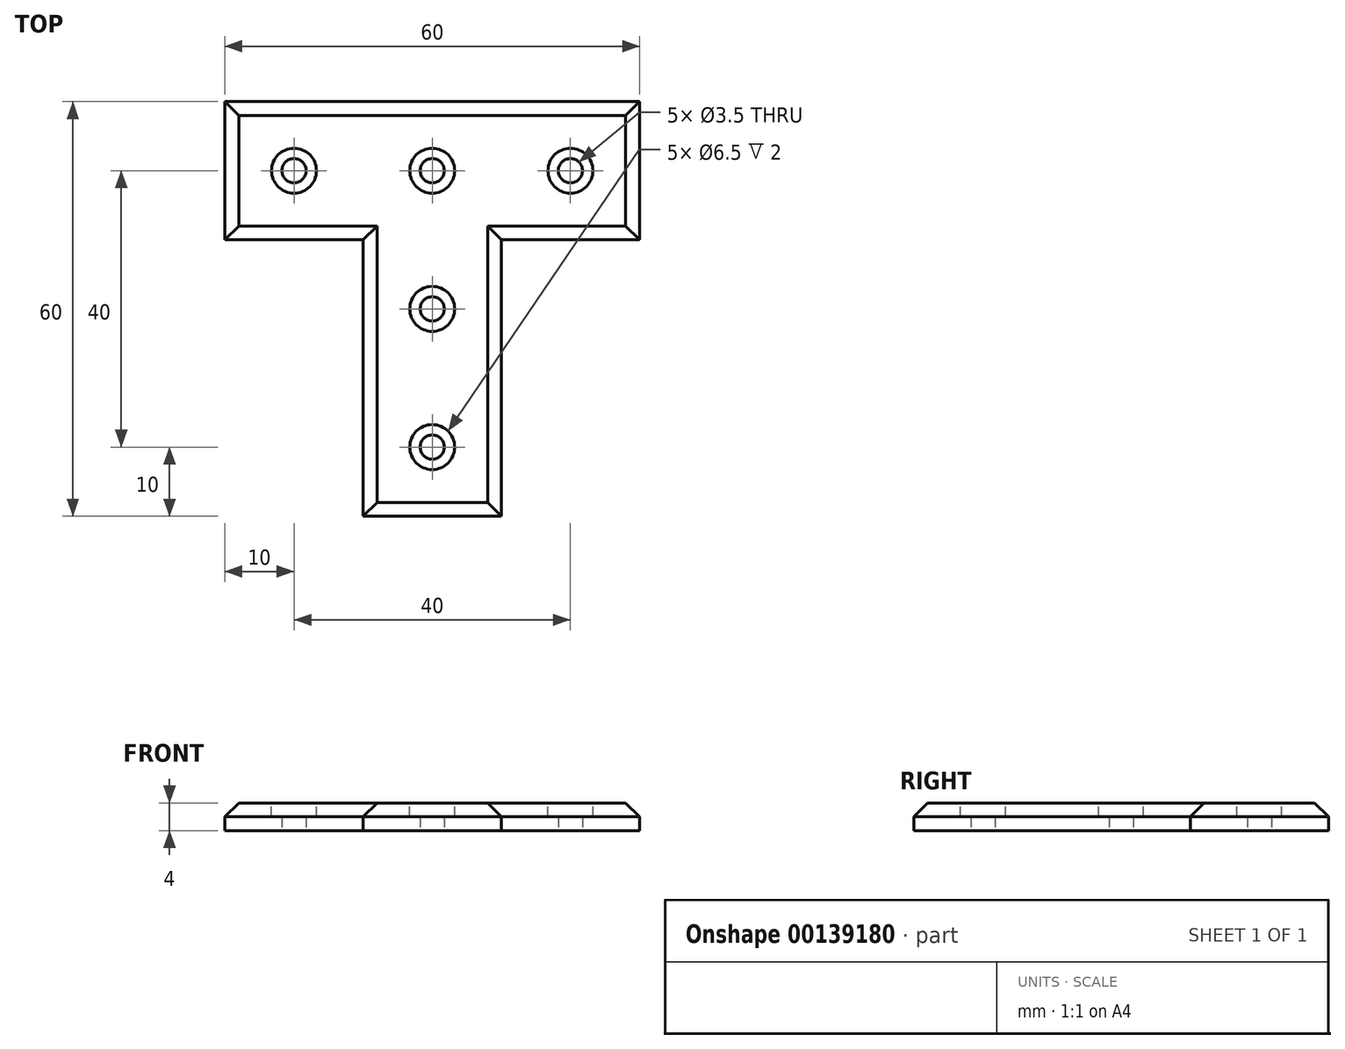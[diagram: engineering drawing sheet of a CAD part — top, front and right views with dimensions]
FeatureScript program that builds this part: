
annotation { "Feature Type Name" : "Feature", "Feature Type Description" : "" }
export const myFeature = defineFeature(function(context is Context, id is Id, definition is map)
    precondition{}
    {
        {
            assignVariable(context, id + "F0", {"name" : "Thickness", "anyValue" : 4});
        }
        {
            assignVariable(context, id + "F1", {"name" : "HeadHeight", "anyValue" : 2});
        }
        {
            var Q0;
            Q0=qCreatedBy(makeId("Top.planeOp"),FACE);
            var sketch = newSketch(context, id + "F2", { "sketchPlane" : qUnion([Q0])});
            skLineSegment(sketch, "E0", {"start": v(0, -50) * mm, "end": v(10, -50) * mm});
            skLineSegment(sketch, "E1", {"start": v(10, -50) * mm, "end": v(10, -10) * mm});
            skLineSegment(sketch, "E2", {"start": v(10, -10) * mm, "end": v(50, -10) * mm});
            skLineSegment(sketch, "E3", {"start": v(50, -10) * mm, "end": v(50, 10) * mm});
            skLineSegment(sketch, "E4", {"start": v(50, 10) * mm, "end": v(0, 10) * mm});
            skLineSegment(sketch, "E5.MirrorCS", {"start": v(-10, -50) * mm, "end": v(-10, -10) * mm});
            skLineSegment(sketch, "E6.MirrorCS", {"start": v(0, -50) * mm, "end": v(-10, -50) * mm});
            skLineSegment(sketch, "E7.MirrorCS", {"start": v(-50, -10) * mm, "end": v(-50, 10) * mm});
            skLineSegment(sketch, "E8.MirrorCS", {"start": v(-10, -10) * mm, "end": v(-50, -10) * mm});
            skLineSegment(sketch, "E9.MirrorCS", {"start": v(-50, 10) * mm, "end": v(0, 10) * mm});
            skCircle(sketch, "E10", {"center": v(0, 0) * mm, "radius": 1.75 * mm});
            skCircle(sketch, "E11", {"center": v(20, 0) * mm, "radius": 1.75 * mm});
            skCircle(sketch, "E12", {"center": v(40, 0) * mm, "radius": 2.25 * mm});
            skCircle(sketch, "E13", {"center": v(0, -20) * mm, "radius": 1.75 * mm});
            skCircle(sketch, "E14", {"center": v(0, -40) * mm, "radius": 1.75 * mm});
            skCircle(sketch, "E15.MirrorC", {"center": v(-40, 0) * mm, "radius": 2.25 * mm});
            skCircle(sketch, "E16.MirrorC", {"center": v(-20, 0) * mm, "radius": 1.75 * mm});
            skLineSegment(sketch, "E17", {"start": v(-30, -10) * mm, "end": v(-30, 10) * mm});
            skLineSegment(sketch, "E18", {"start": v(30, -10) * mm, "end": v(30, 10) * mm});
            skSolve(sketch);
        }
        {
            var Q0;
            Q0=makeQuery(id+"F2.imprint","IMPRINT",FACE,{"disambiguationData":[TD([[makeQuery(id+"F2.imprint","IMPRINT",EDGE,{"derivedFrom":sQuery(id+"F2.wireOp",EDGE,"E0")}),1.0]])]});
            extrude(context, id + "F3", {"entities" : qUnion([Q0]), "depth" : (getVariable(context, 'Thickness')) * mm});
        }
        {
            var Q0;
            Q0=makeQuery(id+"F3.opExtrude","CAP_EDGE",EDGE,{"disambiguationData":[OSD([sQuery(id+"F2.wireOp",EDGE,"E0"),sQuery(id+"F2.wireOp",EDGE,"E6.MirrorCS")])],"isStart":false});
            var Q1;
            Q1=makeQuery(id+"F3.opExtrude","CAP_EDGE",EDGE,{"disambiguationData":[OSD([sQuery(id+"F2.wireOp",EDGE,"E1")])],"isStart":false});
            var Q2;
            Q2=makeQuery(id+"F3.opExtrude","CAP_EDGE",EDGE,{"disambiguationData":[OSD([sQuery(id+"F2.wireOp",EDGE,"E2")])],"isStart":false});
            var Q3;
            Q3=makeQuery(id+"F3.opExtrude","CAP_EDGE",EDGE,{"disambiguationData":[OSD([sQuery(id+"F2.wireOp",EDGE,"E3")])],"isStart":false});
            var Q4;
            Q4=makeQuery(id+"F3.opExtrude","CAP_EDGE",EDGE,{"disambiguationData":[OSD([sQuery(id+"F2.wireOp",EDGE,"E4"),sQuery(id+"F2.wireOp",EDGE,"E9.MirrorCS")])],"isStart":false});
            var Q5;
            Q5=makeQuery(id+"F3.opExtrude","CAP_EDGE",EDGE,{"disambiguationData":[OSD([sQuery(id+"F2.wireOp",EDGE,"E7.MirrorCS")])],"isStart":false});
            var Q6;
            Q6=makeQuery(id+"F3.opExtrude","CAP_EDGE",EDGE,{"disambiguationData":[OSD([sQuery(id+"F2.wireOp",EDGE,"E8.MirrorCS")])],"isStart":false});
            var Q7;
            Q7=makeQuery(id+"F3.opExtrude","CAP_EDGE",EDGE,{"disambiguationData":[OSD([sQuery(id+"F2.wireOp",EDGE,"E5.MirrorCS")])],"isStart":false});
            var Q8;
            Q8=makeQuery(id+"F3.opExtrude","CAP_EDGE",EDGE,{"disambiguationData":[OSD([sQuery(id+"F2.wireOp",EDGE,"E17")])],"isStart":false});
            var Q9;
            Q9=makeQuery(id+"F3.opExtrude","CAP_EDGE",EDGE,{"disambiguationData":[OSD([sQuery(id+"F2.wireOp",EDGE,"E18")])],"isStart":false});
            chamfer(context, id + "F4", {"entities" : qUnion([Q0, Q1, Q2, Q3, Q4, Q5, Q6, Q7, Q8, Q9]), "width" : (getVariable(context, 'Thickness') / 2) * mm, "tangentPropagation" : true});
        }
        {
            var Q0;
            Q0=makeQuery(id+"F3.opExtrude","CAP_FACE",FACE,{"disambiguationData":[OSD([sQuery(id+"F2.wireOp",EDGE,"E0"),sQuery(id+"F2.wireOp",EDGE,"E1"),sQuery(id+"F2.wireOp",EDGE,"E2"),sQuery(id+"F2.wireOp",EDGE,"E4"),sQuery(id+"F2.wireOp",EDGE,"E5.MirrorCS"),sQuery(id+"F2.wireOp",EDGE,"E6.MirrorCS"),sQuery(id+"F2.wireOp",EDGE,"E8.MirrorCS"),sQuery(id+"F2.wireOp",EDGE,"E9.MirrorCS"),sQuery(id+"F2.wireOp",EDGE,"E10"),sQuery(id+"F2.wireOp",EDGE,"E11"),sQuery(id+"F2.wireOp",EDGE,"E13"),sQuery(id+"F2.wireOp",EDGE,"E14"),sQuery(id+"F2.wireOp",EDGE,"E16.MirrorC"),sQuery(id+"F2.wireOp",EDGE,"E17"),sQuery(id+"F2.wireOp",EDGE,"E18")])],"isStart":false});
            var sketch = newSketch(context, id + "F5", { "sketchPlane" : qUnion([Q0])});
            skCircle(sketch, "E19", {"center": v(0, -40) * mm, "radius": 3.25 * mm});
            skCircle(sketch, "E20", {"center": v(0, -20) * mm, "radius": 3.25 * mm});
            skCircle(sketch, "E21", {"center": v(-20, 0) * mm, "radius": 3.25 * mm});
            skCircle(sketch, "E22", {"center": v(0, 0) * mm, "radius": 3.25 * mm});
            skCircle(sketch, "E23", {"center": v(20, 0) * mm, "radius": 3.25 * mm});
            skSolve(sketch);
        }
        {
            var Q0;
            Q0=makeQuery(id+"F5.imprint","IMPRINT",FACE,{"disambiguationData":[TD([[makeQuery(id+"F5.imprint","IMPRINT",EDGE,{"derivedFrom":sQuery(id+"F5.wireOp",EDGE,"E21")}),1.0]])]});
            var Q1;
            Q1=makeQuery(id+"F5.imprint","IMPRINT",FACE,{"disambiguationData":[TD([[makeQuery(id+"F5.imprint","IMPRINT",EDGE,{"derivedFrom":sQuery(id+"F5.wireOp",EDGE,"E22")}),1.0]])]});
            var Q2;
            Q2=makeQuery(id+"F5.imprint","IMPRINT",FACE,{"disambiguationData":[TD([[makeQuery(id+"F5.imprint","IMPRINT",EDGE,{"derivedFrom":sQuery(id+"F5.wireOp",EDGE,"E23")}),1.0]])]});
            var Q3;
            Q3=makeQuery(id+"F5.imprint","IMPRINT",FACE,{"disambiguationData":[TD([[makeQuery(id+"F5.imprint","IMPRINT",EDGE,{"derivedFrom":sQuery(id+"F5.wireOp",EDGE,"E20")}),1.0]])]});
            var Q4;
            Q4=makeQuery(id+"F5.imprint","IMPRINT",FACE,{"disambiguationData":[TD([[makeQuery(id+"F5.imprint","IMPRINT",EDGE,{"derivedFrom":sQuery(id+"F5.wireOp",EDGE,"E19")}),1.0]])]});
            extrude(context, id + "F6", {"entities" : qUnion([Q0, Q1, Q2, Q3, Q4]), "operationType" : NewBodyOperationType.REMOVE, "oppositeDirection" : true, "depth" : (getVariable(context, 'HeadHeight')) * mm});
        }
    });
